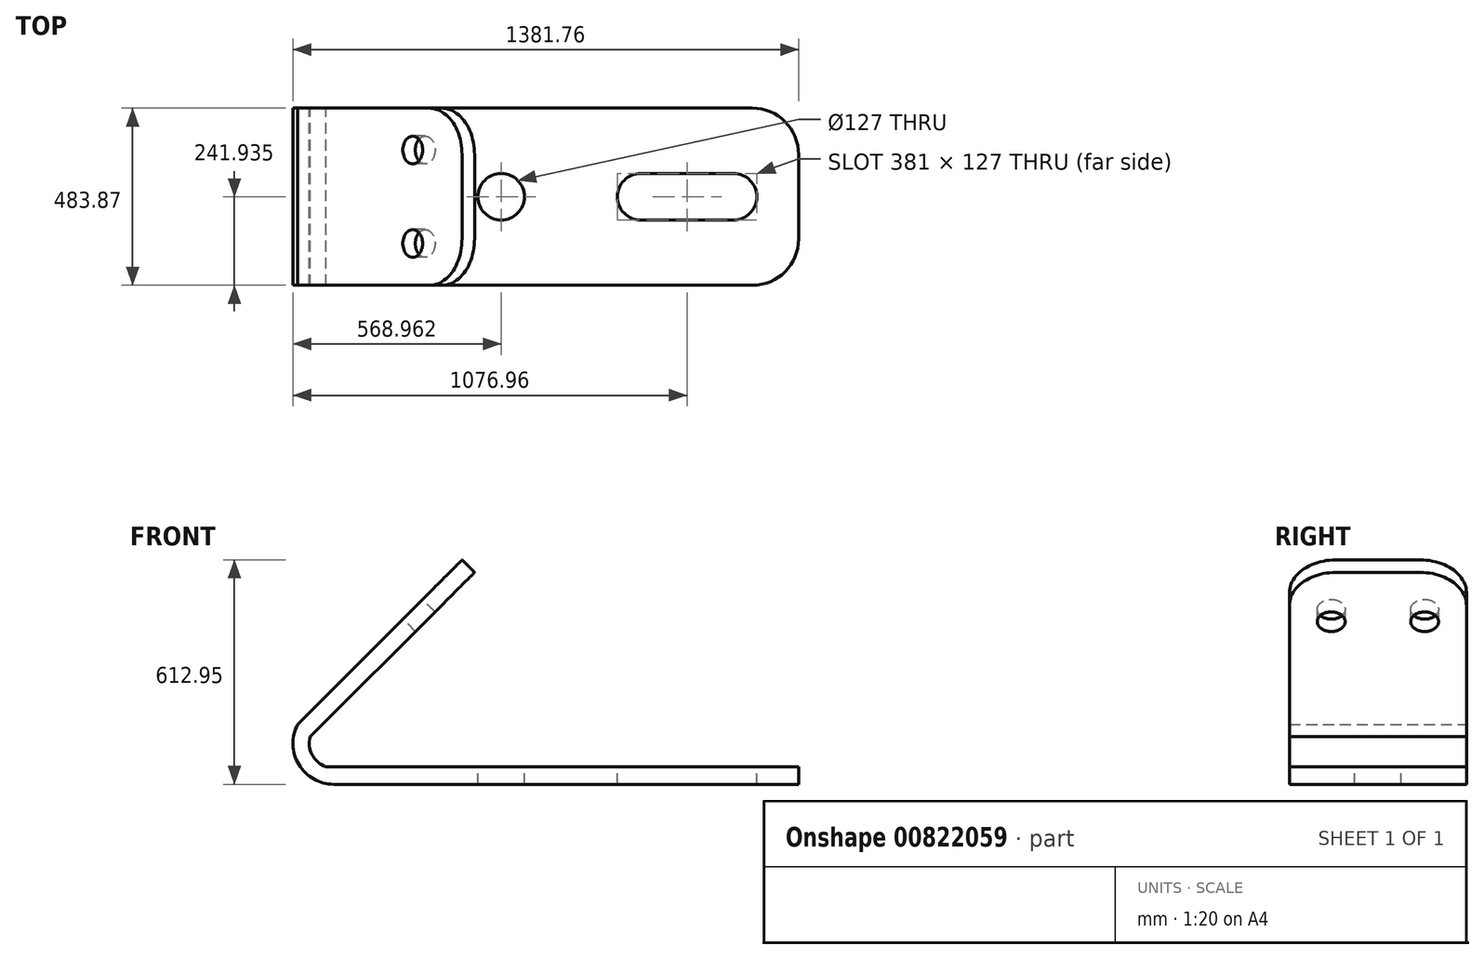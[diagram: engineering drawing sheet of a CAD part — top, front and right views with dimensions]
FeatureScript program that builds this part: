
annotation { "Feature Type Name" : "Feature", "Feature Type Description" : "" }
export const myFeature = defineFeature(function(context is Context, id is Id, definition is map)
    precondition{}
    {
        {
            var Q0;
            Q0=qCreatedBy(makeId("Front.planeOp"),FACE);
            var sketch = newSketch(context, id + "F0", { "sketchPlane" : qUnion([Q0])});
            skLineSegment(sketch, "E0", {"start": v(873.3, -189.29) * mm, "end": v(-396.7, -189.29) * mm});
            skLineSegment(sketch, "E1", {"start": v(-46.52, 423.66) * mm, "end": v(-495.53, -25.36) * mm});
            skLineSegment(sketch, "E2", {"start": v(873.3, -189.29) * mm, "end": v(873.3, -141.03) * mm});
            skLineSegment(sketch, "E3", {"start": v(-46.52, 423.66) * mm, "end": v(-12.4, 389.53) * mm});
            skLineSegment(sketch, "E4", {"start": v(-418.63, -141.03) * mm, "end": v(873.3, -141.03) * mm});
            skLineSegment(sketch, "E5", {"start": v(-12.4, 389.53) * mm, "end": v(-461.4, -59.48) * mm});
            skArc(sketch, "E6", {"start": v(-495.53, -25.36) * mm, "mid": v(-492.4, -135.23) * mm, "end": v(-396.7, -189.29) * mm});
            skArc(sketch, "E7", {"start": v(-418.63, -141.03) * mm, "mid": v(-456.19, -108.74) * mm, "end": v(-461.4, -59.48) * mm});
            skSolve(sketch);
        }
        {
            var Q0;
            Q0=makeQuery(id+"F0.imprint","IMPRINT",FACE,{"disambiguationData":[TD([[makeQuery(id+"F0.imprint","IMPRINT",EDGE,{"derivedFrom":sQuery(id+"F0.wireOp",EDGE,"E0")}),-1.0]])]});
            extrude(context, id + "F1", {"entities" : qUnion([Q0]), "depth" : 483.87 * mm, "offsetDistance" : 25.4 * mm});
        }
        {
            var Q0;
            Q0=makeQuery(id+"F1.opExtrude","SWEPT_FACE",FACE,{"disambiguationData":[OSD([sQuery(id+"F0.wireOp",EDGE,"E4")])]});
            var sketch = newSketch(context, id + "F2", { "sketchPlane" : qUnion([Q0])});
            skPoint(sketch, "E8.start.orphan", {"position": v(873.3, -241.94) * mm});
            skCircle(sketch, "E9", {"center": v(60.5, -241.94) * mm, "radius": 63.5 * mm});
            skArc(sketch, "E10", {"start": v(695.5, -305.44) * mm, "mid": v(759, -241.94) * mm, "end": v(695.5, -178.44) * mm});
            skArc(sketch, "E11", {"start": v(441.5, -178.44) * mm, "mid": v(378, -241.94) * mm, "end": v(441.5, -305.44) * mm});
            skLineSegment(sketch, "E12", {"start": v(441.5, -178.44) * mm, "end": v(695.5, -178.44) * mm});
            skLineSegment(sketch, "E13", {"start": v(441.5, -305.44) * mm, "end": v(695.5, -305.44) * mm});
            skSolve(sketch);
        }
        {
            var Q0;
            Q0=makeQuery(id+"F2.imprint","IMPRINT",FACE,{"disambiguationData":[TD([[makeQuery(id+"F2.imprint","IMPRINT",EDGE,{"derivedFrom":sQuery(id+"F2.wireOp",EDGE,"E10")}),1.0]])]});
            var Q1;
            Q1=makeQuery(id+"F2.imprint","IMPRINT",FACE,{"disambiguationData":[TD([[makeQuery(id+"F2.imprint","IMPRINT",EDGE,{"derivedFrom":sQuery(id+"F2.wireOp",EDGE,"E9")}),1.0]])]});
            extrude(context, id + "F3", {"entities" : qUnion([Q0, Q1]), "operationType" : NewBodyOperationType.REMOVE, "oppositeDirection" : true, "depth" : 137.16 * mm, "offsetDistance" : 25.4 * mm});
        }
        {
            var Q0;
            Q0=makeQuery(id+"F1.opExtrude","CAP_EDGE",EDGE,{"disambiguationData":[OSD([sQuery(id+"F0.wireOp",EDGE,"E2")])],"isStart":false});
            var Q1;
            Q1=makeQuery(id+"F1.opExtrude","CAP_EDGE",EDGE,{"disambiguationData":[OSD([sQuery(id+"F0.wireOp",EDGE,"E2")])],"isStart":true});
            fillet(context, id + "F4", {"entities" : qUnion([Q0, Q1]), "radius" : 127 * mm, "tangentPropagation" : true, "allowEdgeOverflow" : false});
        }
        {
            var Q0;
            Q0=makeQuery(id+"F1.opExtrude","SWEPT_FACE",FACE,{"disambiguationData":[OSD([sQuery(id+"F0.wireOp",EDGE,"E1")])]});
            var sketch = newSketch(context, id + "F5", { "sketchPlane" : qUnion([Q0])});
            skLineSegment(sketch, "E14", {"start": v(0, -368.32) * mm, "end": v(114.3, -368.32) * mm});
            skLineSegment(sketch, "E15", {"start": v(483.87, -368.32) * mm, "end": v(369.57, -368.32) * mm});
            skCircle(sketch, "E16", {"center": v(114.3, 76.18) * mm, "radius": 38.1 * mm});
            skCircle(sketch, "E17", {"center": v(369.57, 76.18) * mm, "radius": 38.1 * mm});
            skSolve(sketch);
        }
        {
            var Q0;
            Q0=makeQuery(id+"F5.imprint","IMPRINT",FACE,{"disambiguationData":[TD([[makeQuery(id+"F5.imprint","IMPRINT",EDGE,{"derivedFrom":sQuery(id+"F5.wireOp",EDGE,"E17")}),1.0]])]});
            var Q1;
            Q1=makeQuery(id+"F5.imprint","IMPRINT",FACE,{"disambiguationData":[TD([[makeQuery(id+"F5.imprint","IMPRINT",EDGE,{"derivedFrom":sQuery(id+"F5.wireOp",EDGE,"E16")}),1.0]])]});
            extrude(context, id + "F6", {"entities" : qUnion([Q0, Q1]), "operationType" : NewBodyOperationType.REMOVE, "oppositeDirection" : true, "depth" : 81.28 * mm, "offsetDistance" : 25.4 * mm});
        }
        {
            var Q0;
            Q0=makeQuery(id+"F1.opExtrude","CAP_EDGE",EDGE,{"disambiguationData":[OSD([sQuery(id+"F0.wireOp",EDGE,"E3")])],"isStart":false});
            var Q1;
            Q1=makeQuery(id+"F1.opExtrude","CAP_EDGE",EDGE,{"disambiguationData":[OSD([sQuery(id+"F0.wireOp",EDGE,"E3")])],"isStart":true});
            fillet(context, id + "F7", {"entities" : qUnion([Q0, Q1]), "radius" : 127 * mm, "tangentPropagation" : true, "allowEdgeOverflow" : false});
        }
    });
